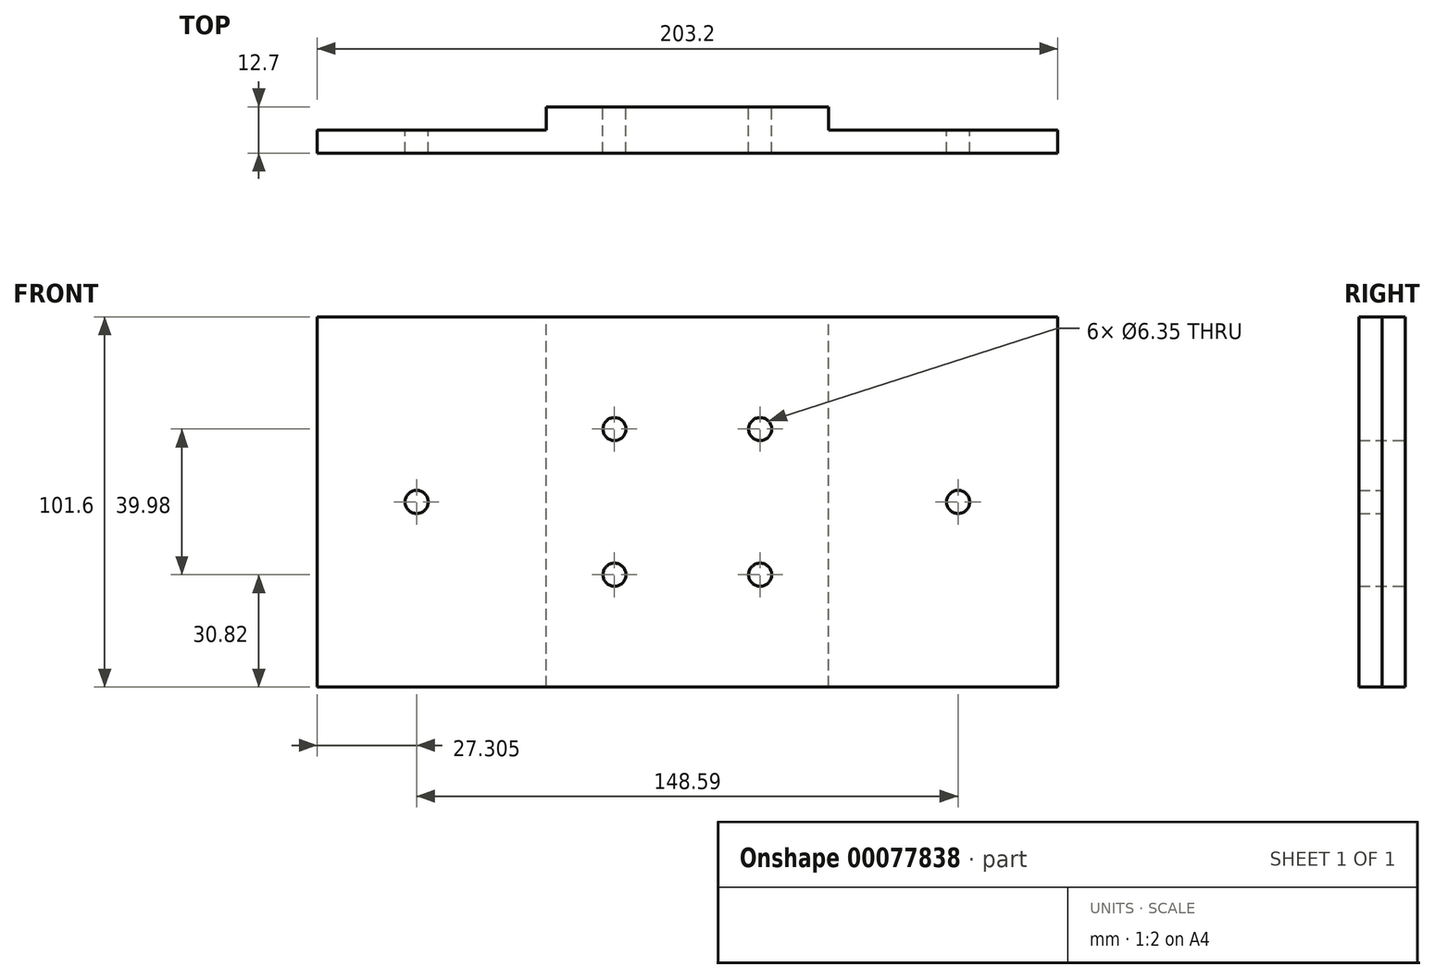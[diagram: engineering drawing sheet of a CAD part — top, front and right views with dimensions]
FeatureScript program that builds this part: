
annotation { "Feature Type Name" : "Feature", "Feature Type Description" : "" }
export const myFeature = defineFeature(function(context is Context, id is Id, definition is map)
    precondition{}
    {
        {
            var Q0;
            Q0=qCreatedBy(makeId("Front.planeOp"),FACE);
            var sketch = newSketch(context, id + "F0", { "sketchPlane" : qUnion([Q0])});
            skLineSegment(sketch, "E0.bottom", {"start": v(-101.6, 50.8) * mm, "end": v(101.6, 50.8) * mm});
            skLineSegment(sketch, "E0.top", {"start": v(-101.6, -50.8) * mm, "end": v(101.6, -50.8) * mm});
            skLineSegment(sketch, "E0.left", {"start": v(-101.6, 50.8) * mm, "end": v(-101.6, -50.8) * mm});
            skLineSegment(sketch, "E0.right", {"start": v(101.6, 50.8) * mm, "end": v(101.6, -50.8) * mm});
            skPoint(sketch, "E0.middle", {"position": v(0, 0) * mm});
            skLineSegment(sketch, "E1", {"start": v(0, 50.8) * mm, "end": v(0, -50.8) * mm});
            skLineSegment(sketch, "E2", {"start": v(-101.6, 0) * mm, "end": v(101.6, 0) * mm});
            skCircle(sketch, "E3", {"center": v(-20, 20) * mm, "radius": 3.18 * mm});
            skCircle(sketch, "E4.0.1.0", {"center": v(-20, -19.98) * mm, "radius": 3.18 * mm});
            skCircle(sketch, "E4.1.0.0", {"center": v(19.98, 20) * mm, "radius": 3.18 * mm});
            skCircle(sketch, "E4.1.1.0", {"center": v(19.98, -19.98) * mm, "radius": 3.18 * mm});
            skLineSegment(sketch, "E4.direction1", {"start": v(-20, 20) * mm, "end": v(19.98, 20) * mm, "construction": true});
            skLineSegment(sketch, "E4.direction2", {"start": v(-20, 20) * mm, "end": v(-20, -19.98) * mm, "construction": true});
            skCircle(sketch, "E5", {"center": v(-74.3, 0) * mm, "radius": 3.18 * mm});
            skCircle(sketch, "E6", {"center": v(74.3, 0) * mm, "radius": 3.18 * mm});
            skSolve(sketch);
        }
        {
            var Q0;
            Q0 = qSketchRegion(id + "F0", true);
            extrude(context, id + "F1", {"entities" : qUnion([Q0]), "depth" : 12.7 * mm});
        }
        {
            var Q0;
            Q0=makeQuery(id+"F1.opExtrude","SWEPT_FACE",FACE,{"disambiguationData":[OSD([sQuery(id+"F0.wireOp",EDGE,"E0.bottom")])]});
            var sketch = newSketch(context, id + "F2", { "sketchPlane" : qUnion([Q0])});
            skLineSegment(sketch, "E7", {"start": v(-38.75, 0) * mm, "end": v(-38.75, -12.7) * mm});
            skLineSegment(sketch, "E8", {"start": v(38.75, 0) * mm, "end": v(38.75, -12.7) * mm});
            skLineSegment(sketch, "E9", {"start": v(-38.75, -6.35) * mm, "end": v(-101.6, -6.35) * mm});
            skLineSegment(sketch, "E10", {"start": v(38.75, -6.35) * mm, "end": v(101.6, -6.35) * mm});
            skSolve(sketch);
        }
        {
            var Q0;
            {var subQ4=sQuery(id+"F2.wireOp",EDGE,"E9");Q0=makeQuery(id+"F2.imprint","IMPRINT",FACE,{"disambiguationData":[TD([[makeQuery(id+"F2.imprint","IMPRINT",EDGE,{"derivedFrom":subQ4}),-1.0]])]});}
            extrude(context, id + "F3", {"entities" : qUnion([Q0]), "operationType" : NewBodyOperationType.REMOVE, "endBound" : BoundingType.THROUGH_ALL, "oppositeDirection" : true, "depth" : 25.4 * mm});
        }
        {
            var Q0;
            {var subQ4=sQuery(id+"F2.wireOp",EDGE,"E10");Q0=makeQuery(id+"F2.imprint","IMPRINT",FACE,{"disambiguationData":[TD([[makeQuery(id+"F2.imprint","IMPRINT",EDGE,{"derivedFrom":subQ4}),1.0]])]});}
            extrude(context, id + "F4", {"entities" : qUnion([Q0]), "operationType" : NewBodyOperationType.REMOVE, "endBound" : BoundingType.THROUGH_ALL, "oppositeDirection" : true, "depth" : 25.4 * mm});
        }
    });
